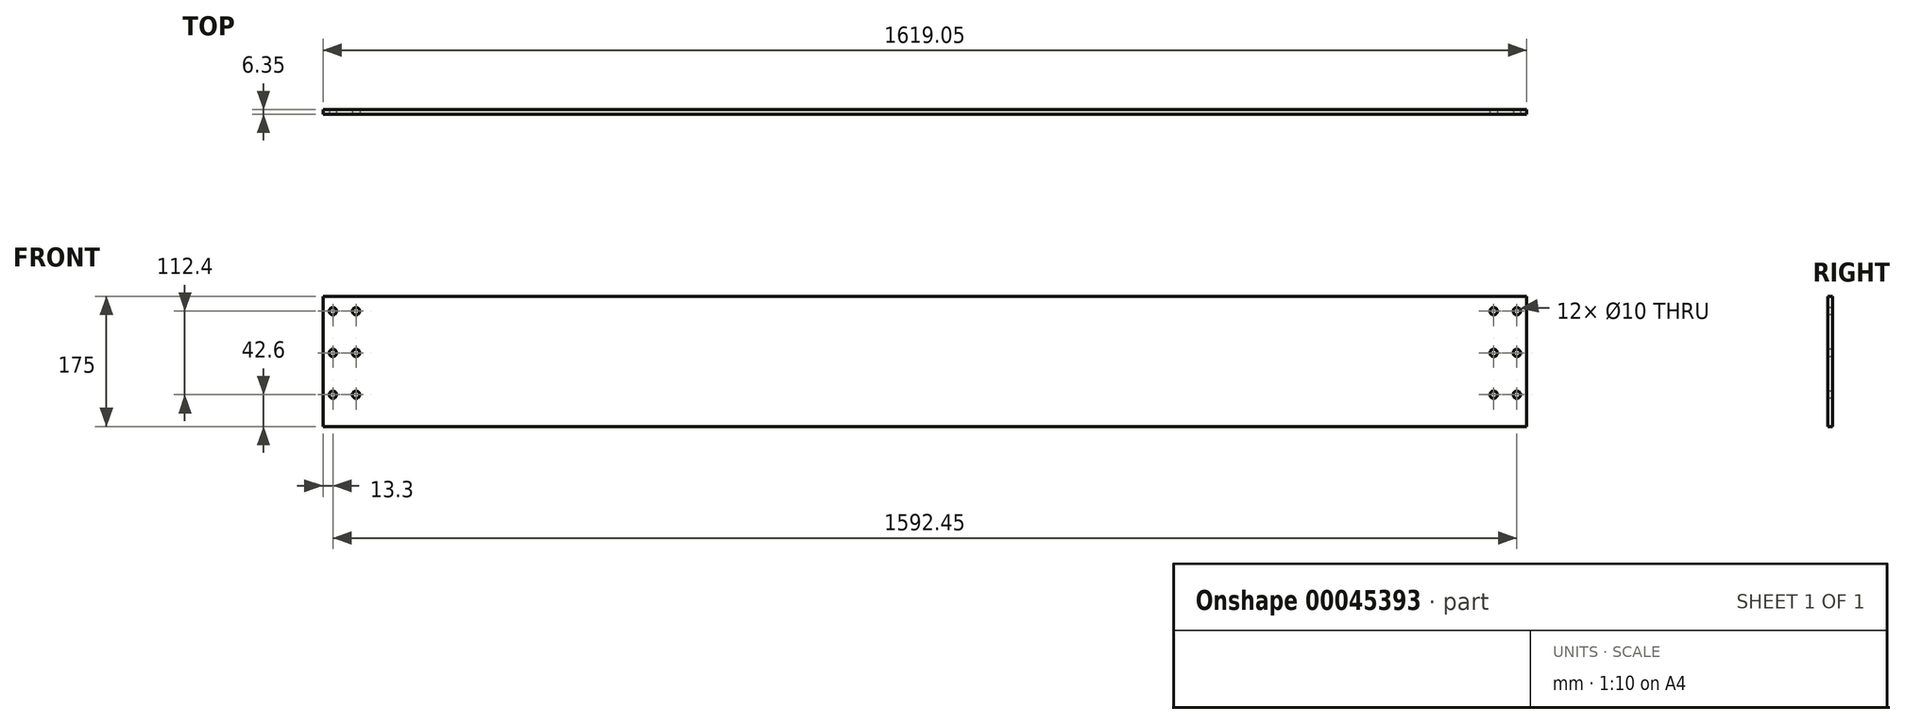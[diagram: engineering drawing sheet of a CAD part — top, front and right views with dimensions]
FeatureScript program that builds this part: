
annotation { "Feature Type Name" : "Feature", "Feature Type Description" : "" }
export const myFeature = defineFeature(function(context is Context, id is Id, definition is map)
    precondition{}
    {
        {
            var Q0;
            Q0=qCreatedBy(makeId("Front.planeOp"),FACE);
            var sketch = newSketch(context, id + "F0", { "sketchPlane" : qUnion([Q0])});
            skLineSegment(sketch, "E0.bottom", {"start": v(-169.96, 96.37) * mm, "end": v(1449.09, 96.37) * mm});
            skLineSegment(sketch, "E0.top", {"start": v(-169.96, -78.63) * mm, "end": v(1449.09, -78.63) * mm});
            skLineSegment(sketch, "E0.left", {"start": v(-169.96, 96.37) * mm, "end": v(-169.96, -78.63) * mm});
            skLineSegment(sketch, "E0.right", {"start": v(1449.09, 96.37) * mm, "end": v(1449.09, -78.63) * mm});
            skSolve(sketch);
        }
        {
            var Q0;
            Q0=makeQuery(id+"F0.imprint","IMPRINT",FACE,{"disambiguationData":[TD([[makeQuery(id+"F0.imprint","IMPRINT",EDGE,{"derivedFrom":sQuery(id+"F0.wireOp",EDGE,"E0.bottom")}),-1.0]])]});
            extrude(context, id + "F1", {"entities" : qUnion([Q0]), "depth" : 6.35 * mm});
        }
        {
            var Q0;
            Q0=makeQuery(id+"F1.opExtrude","CAP_FACE",FACE,{"disambiguationData":[OSD([sQuery(id+"F0.wireOp",EDGE,"E0.bottom"),sQuery(id+"F0.wireOp",EDGE,"E0.top"),sQuery(id+"F0.wireOp",EDGE,"E0.left"),sQuery(id+"F0.wireOp",EDGE,"E0.right")])],"isStart":false});
            var sketch = newSketch(context, id + "F2", { "sketchPlane" : qUnion([Q0])});
            skCircle(sketch, "E1", {"center": v(-156.66, 76.37) * mm, "radius": 5 * mm});
            skCircle(sketch, "E2.0.1.0", {"center": v(-156.66, 20.17) * mm, "radius": 5 * mm});
            skCircle(sketch, "E2.0.2.0", {"center": v(-156.66, -36.03) * mm, "radius": 5 * mm});
            skCircle(sketch, "E2.1.0.0", {"center": v(-125.46, 76.37) * mm, "radius": 5 * mm});
            skCircle(sketch, "E2.1.1.0", {"center": v(-125.46, 20.17) * mm, "radius": 5 * mm});
            skCircle(sketch, "E2.1.2.0", {"center": v(-125.46, -36.03) * mm, "radius": 5 * mm});
            skLineSegment(sketch, "E2.direction1", {"start": v(-156.66, 76.37) * mm, "end": v(-125.46, 76.37) * mm, "construction": true});
            skLineSegment(sketch, "E2.direction2", {"start": v(-156.66, 76.37) * mm, "end": v(-156.66, 20.17) * mm, "construction": true});
            skCircle(sketch, "E3", {"center": v(1435.79, 76.37) * mm, "radius": 5 * mm});
            skCircle(sketch, "E4.0.1.0", {"center": v(1435.79, 20.17) * mm, "radius": 5 * mm});
            skCircle(sketch, "E4.0.2.0", {"center": v(1435.79, -36.03) * mm, "radius": 5 * mm});
            skCircle(sketch, "E4.1.0.0", {"center": v(1404.59, 76.37) * mm, "radius": 5 * mm});
            skCircle(sketch, "E4.1.1.0", {"center": v(1404.59, 20.17) * mm, "radius": 5 * mm});
            skCircle(sketch, "E4.1.2.0", {"center": v(1404.59, -36.03) * mm, "radius": 5 * mm});
            skLineSegment(sketch, "E4.direction1", {"start": v(1435.79, 76.37) * mm, "end": v(1404.59, 76.37) * mm, "construction": true});
            skLineSegment(sketch, "E4.direction2", {"start": v(1435.79, 76.37) * mm, "end": v(1435.79, 20.17) * mm, "construction": true});
            skSolve(sketch);
        }
        {
            var Q0;
            Q0=makeQuery(id+"F2.imprint","IMPRINT",FACE,{"disambiguationData":[TD([[makeQuery(id+"F2.imprint","IMPRINT",EDGE,{"derivedFrom":sQuery(id+"F2.wireOp",EDGE,"E2.0.1.0")}),1.0]])]});
            var Q1;
            Q1=makeQuery(id+"F2.imprint","IMPRINT",FACE,{"disambiguationData":[TD([[makeQuery(id+"F2.imprint","IMPRINT",EDGE,{"derivedFrom":sQuery(id+"F2.wireOp",EDGE,"E2.0.2.0")}),1.0]])]});
            var Q2;
            Q2=makeQuery(id+"F2.imprint","IMPRINT",FACE,{"disambiguationData":[TD([[makeQuery(id+"F2.imprint","IMPRINT",EDGE,{"derivedFrom":sQuery(id+"F2.wireOp",EDGE,"E2.1.0.0")}),1.0]])]});
            var Q3;
            Q3=makeQuery(id+"F2.imprint","IMPRINT",FACE,{"disambiguationData":[TD([[makeQuery(id+"F2.imprint","IMPRINT",EDGE,{"derivedFrom":sQuery(id+"F2.wireOp",EDGE,"E2.1.1.0")}),1.0]])]});
            var Q4;
            Q4=makeQuery(id+"F2.imprint","IMPRINT",FACE,{"disambiguationData":[TD([[makeQuery(id+"F2.imprint","IMPRINT",EDGE,{"derivedFrom":sQuery(id+"F2.wireOp",EDGE,"E2.1.2.0")}),1.0]])]});
            var Q5;
            Q5=makeQuery(id+"F2.imprint","IMPRINT",FACE,{"disambiguationData":[TD([[makeQuery(id+"F2.imprint","IMPRINT",EDGE,{"derivedFrom":sQuery(id+"F2.wireOp",EDGE,"E1")}),1.0]])]});
            var Q6;
            Q6=makeQuery(id+"F2.imprint","IMPRINT",FACE,{"disambiguationData":[TD([[makeQuery(id+"F2.imprint","IMPRINT",EDGE,{"derivedFrom":sQuery(id+"F2.wireOp",EDGE,"E4.1.0.0")}),1.0]])]});
            var Q7;
            Q7=makeQuery(id+"F2.imprint","IMPRINT",FACE,{"disambiguationData":[TD([[makeQuery(id+"F2.imprint","IMPRINT",EDGE,{"derivedFrom":sQuery(id+"F2.wireOp",EDGE,"E3")}),1.0]])]});
            var Q8;
            Q8=makeQuery(id+"F2.imprint","IMPRINT",FACE,{"disambiguationData":[TD([[makeQuery(id+"F2.imprint","IMPRINT",EDGE,{"derivedFrom":sQuery(id+"F2.wireOp",EDGE,"E4.1.1.0")}),1.0]])]});
            var Q9;
            Q9=makeQuery(id+"F2.imprint","IMPRINT",FACE,{"disambiguationData":[TD([[makeQuery(id+"F2.imprint","IMPRINT",EDGE,{"derivedFrom":sQuery(id+"F2.wireOp",EDGE,"E4.0.1.0")}),1.0]])]});
            var Q10;
            Q10=makeQuery(id+"F2.imprint","IMPRINT",FACE,{"disambiguationData":[TD([[makeQuery(id+"F2.imprint","IMPRINT",EDGE,{"derivedFrom":sQuery(id+"F2.wireOp",EDGE,"E4.0.2.0")}),1.0]])]});
            var Q11;
            Q11=makeQuery(id+"F2.imprint","IMPRINT",FACE,{"disambiguationData":[TD([[makeQuery(id+"F2.imprint","IMPRINT",EDGE,{"derivedFrom":sQuery(id+"F2.wireOp",EDGE,"E4.1.2.0")}),1.0]])]});
            extrude(context, id + "F3", {"entities" : qUnion([Q0, Q1, Q2, Q3, Q4, Q5, Q6, Q7, Q8, Q9, Q10, Q11]), "operationType" : NewBodyOperationType.REMOVE, "oppositeDirection" : true, "depth" : 25 * mm});
        }
    });
